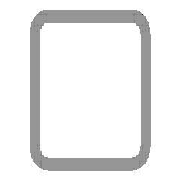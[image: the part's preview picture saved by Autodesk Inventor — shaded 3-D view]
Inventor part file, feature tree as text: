
AUTODESK INVENTOR PART (.ipt)
format: ipt  version: 2016 (Build 200138000, 138)  size: 128,512 bytes
history: native  units: mm (DEFAULTED — no unit token found)
features: other x4, sketch x3, plane x1
ambient origin geometry x8: Origin, YZ Plane, XZ Plane, XY Plane, X Axis, Y Axis, Z Axis, Center Point
bodies: Solid1 (feature_tree), Body (feature_tree)
feature tree (8):
  parser-record x1  (decoder bookkeeping rows leaked as tree rows — omitted from the tree; the rows remain in map.json)
  other  "Driven Length"
  other  "Start plane"
  other  "End plane"
  sketch  "Sketch"  dims[d7=4.0mm d9=60.0mm d11=60.0mm d12=2.0mm d13=-0.0mm d14=463.182711mm d15=30.0mm d16=30.0mm d17=90.0deg d18=463.182711mm]
  sketch  "Sketch3"  dims[d3=463.182711mm]
  plane  "Work Plane3"
  sketch  "Sketch4"  dims[d4=0.0mm]
